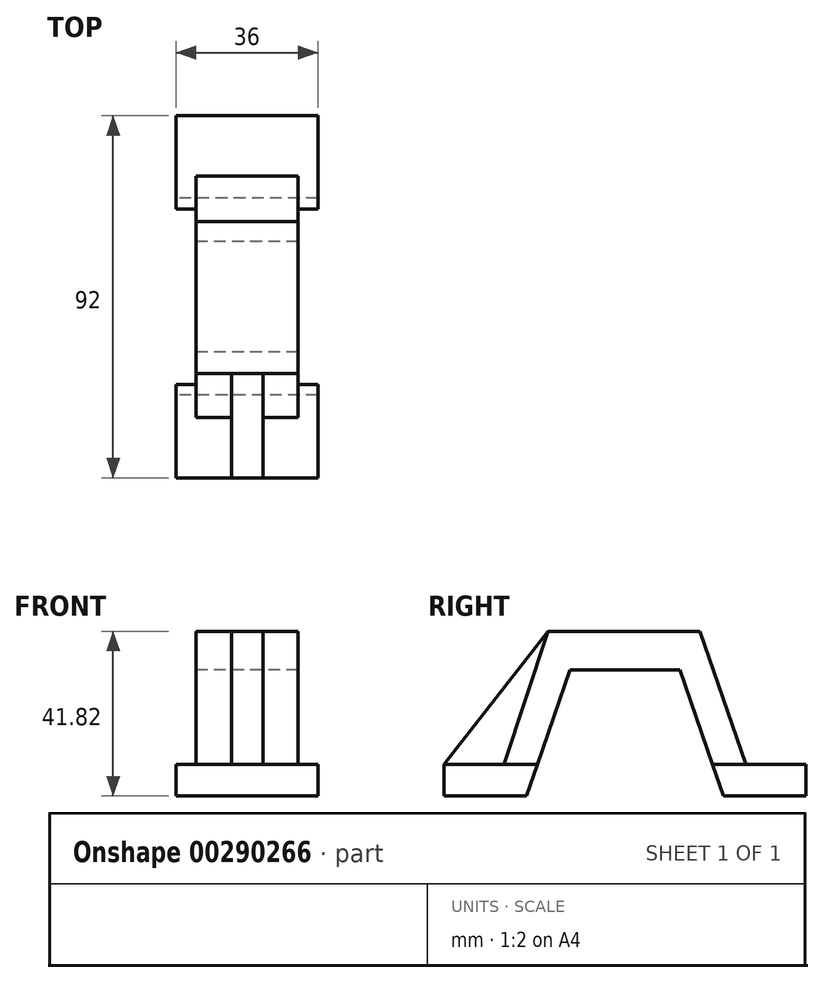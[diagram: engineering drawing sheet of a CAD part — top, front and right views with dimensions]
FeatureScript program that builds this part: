
annotation { "Feature Type Name" : "Feature", "Feature Type Description" : "" }
export const myFeature = defineFeature(function(context is Context, id is Id, definition is map)
    precondition{}
    {
        {
            var Q0;
            Q0=qCreatedBy(makeId("Right.planeOp"),FACE);
            var sketch = newSketch(context, id + "F0", { "sketchPlane" : qUnion([Q0])});
            skLineSegment(sketch, "E0", {"start": v(-64.15, 0) * mm, "end": v(-43.15, 0) * mm});
            skLineSegment(sketch, "E1", {"start": v(6.85, 0) * mm, "end": v(27.85, 0) * mm});
            skLineSegment(sketch, "E2", {"start": v(-32.15, 32) * mm, "end": v(-43.15, 0) * mm});
            skLineSegment(sketch, "E3", {"start": v(-32.15, 32) * mm, "end": v(-4.15, 32) * mm});
            skLineSegment(sketch, "E4", {"start": v(-4.15, 32) * mm, "end": v(6.85, 0) * mm});
            skLineSegment(sketch, "E5", {"start": v(-64.15, 0) * mm, "end": v(-64.15, 8) * mm});
            skLineSegment(sketch, "E6", {"start": v(-48.86, 8) * mm, "end": v(-64.15, 8) * mm});
            skLineSegment(sketch, "E7", {"start": v(-48.86, 8) * mm, "end": v(-37.69, 41.82) * mm});
            skLineSegment(sketch, "E8", {"start": v(-37.69, 41.82) * mm, "end": v(0.94, 41.82) * mm});
            skLineSegment(sketch, "E9", {"start": v(27.85, 0) * mm, "end": v(27.85, 8) * mm});
            skLineSegment(sketch, "E10", {"start": v(0.94, 41.82) * mm, "end": v(12.56, 8) * mm});
            skLineSegment(sketch, "E11", {"start": v(12.56, 8) * mm, "end": v(27.85, 8) * mm});
            skLineSegment(sketch, "E12", {"start": v(-64.15, 8) * mm, "end": v(-37.69, 41.82) * mm});
            skLineSegment(sketch, "E13", {"start": v(0.94, 41.82) * mm, "end": v(0.94, 66.82) * mm});
            skLineSegment(sketch, "E14", {"start": v(0.94, 66.82) * mm, "end": v(-28.06, 66.82) * mm});
            skLineSegment(sketch, "E15", {"start": v(-28.06, 66.82) * mm, "end": v(-28.06, 41.82) * mm});
            skSolve(sketch);
        }
        {
            var Q0;
            Q0=makeQuery(id+"F0.imprint","IMPRINT",FACE,{"disambiguationData":[TD([[makeQuery(id+"F0.imprint","IMPRINT",EDGE,{"derivedFrom":sQuery(id+"F0.wireOp",EDGE,"E0")}),1.0]])]});
            extrude(context, id + "F1", {"entities" : qUnion([Q0]), "depth" : 36 * mm});
        }
        {
            var Q0;
            Q0=makeQuery(id+"F1.opExtrude","CAP_FACE",FACE,{"disambiguationData":[OSD([sQuery(id+"F0.wireOp",EDGE,"E0"),sQuery(id+"F0.wireOp",EDGE,"E1"),sQuery(id+"F0.wireOp",EDGE,"E2"),sQuery(id+"F0.wireOp",EDGE,"E3"),sQuery(id+"F0.wireOp",EDGE,"E4"),sQuery(id+"F0.wireOp",EDGE,"E5"),sQuery(id+"F0.wireOp",EDGE,"E6"),sQuery(id+"F0.wireOp",EDGE,"E7"),sQuery(id+"F0.wireOp",EDGE,"E8"),sQuery(id+"F0.wireOp",EDGE,"E9"),sQuery(id+"F0.wireOp",EDGE,"E10"),sQuery(id+"F0.wireOp",EDGE,"E11")])],"isStart":false});
            var sketch = newSketch(context, id + "F2", { "sketchPlane" : qUnion([Q0])});
            skLineSegment(sketch, "E16", {"start": v(-48.86, 8) * mm, "end": v(-40.4, 8) * mm});
            skLineSegment(sketch, "E17", {"start": v(12.56, 8) * mm, "end": v(4.1, 8) * mm});
            skLineSegment(sketch, "E18", {"start": v(-48.86, 8) * mm, "end": v(-37.69, 41.82) * mm});
            skLineSegment(sketch, "E19", {"start": v(-37.69, 41.82) * mm, "end": v(0.94, 41.82) * mm});
            skLineSegment(sketch, "E20", {"start": v(0.94, 41.82) * mm, "end": v(12.56, 8) * mm});
            skLineSegment(sketch, "E21", {"start": v(4.1, 8) * mm, "end": v(-4.15, 32) * mm});
            skLineSegment(sketch, "E22", {"start": v(-4.15, 32) * mm, "end": v(-32.15, 32) * mm});
            skLineSegment(sketch, "E23", {"start": v(-32.15, 32) * mm, "end": v(-40.4, 8) * mm});
            skSolve(sketch);
        }
        {
            var Q0;
            Q0=makeQuery(id+"F2.imprint","IMPRINT",FACE,{"disambiguationData":[TD([[makeQuery(id+"F2.imprint","IMPRINT",EDGE,{"derivedFrom":sQuery(id+"F2.wireOp",EDGE,"E16")}),1.0]])]});
            extrude(context, id + "F3", {"entities" : qUnion([Q0]), "operationType" : NewBodyOperationType.REMOVE, "oppositeDirection" : true, "depth" : 5 * mm});
        }
        {
            var Q0;
            Q0=makeQuery(id+"F1.opExtrude","CAP_FACE",FACE,{"disambiguationData":[OSD([sQuery(id+"F0.wireOp",EDGE,"E0"),sQuery(id+"F0.wireOp",EDGE,"E1"),sQuery(id+"F0.wireOp",EDGE,"E2"),sQuery(id+"F0.wireOp",EDGE,"E3"),sQuery(id+"F0.wireOp",EDGE,"E4"),sQuery(id+"F0.wireOp",EDGE,"E5"),sQuery(id+"F0.wireOp",EDGE,"E6"),sQuery(id+"F0.wireOp",EDGE,"E7"),sQuery(id+"F0.wireOp",EDGE,"E8"),sQuery(id+"F0.wireOp",EDGE,"E9"),sQuery(id+"F0.wireOp",EDGE,"E10"),sQuery(id+"F0.wireOp",EDGE,"E11")])],"isStart":true});
            var sketch = newSketch(context, id + "F4", { "sketchPlane" : qUnion([Q0])});
            skLineSegment(sketch, "E24", {"start": v(-12.56, 8) * mm, "end": v(-4.1, 8) * mm});
            skLineSegment(sketch, "E25", {"start": v(-4.1, 8) * mm, "end": v(4.15, 32) * mm});
            skLineSegment(sketch, "E26", {"start": v(4.15, 32) * mm, "end": v(32.15, 32) * mm});
            skLineSegment(sketch, "E27", {"start": v(32.15, 32) * mm, "end": v(40.4, 8) * mm});
            skLineSegment(sketch, "E28", {"start": v(40.4, 8) * mm, "end": v(48.86, 8) * mm});
            skLineSegment(sketch, "E29", {"start": v(48.86, 8) * mm, "end": v(37.69, 41.82) * mm});
            skLineSegment(sketch, "E30", {"start": v(37.69, 41.82) * mm, "end": v(-0.94, 41.82) * mm});
            skLineSegment(sketch, "E31", {"start": v(-0.94, 41.82) * mm, "end": v(-12.56, 8) * mm});
            skSolve(sketch);
        }
        {
            var Q0;
            Q0=makeQuery(id+"F4.imprint","IMPRINT",FACE,{"disambiguationData":[TD([[makeQuery(id+"F4.imprint","IMPRINT",EDGE,{"derivedFrom":sQuery(id+"F4.wireOp",EDGE,"E24")}),1.0]])]});
            extrude(context, id + "F5", {"entities" : qUnion([Q0]), "operationType" : NewBodyOperationType.REMOVE, "oppositeDirection" : true, "depth" : 5 * mm});
        }
        {
            var Q0;
            Q0=makeQuery(id+"F0.imprint","IMPRINT",FACE,{"disambiguationData":[TD([[makeQuery(id+"F0.imprint","IMPRINT",EDGE,{"derivedFrom":sQuery(id+"F0.wireOp",EDGE,"E6")}),-1.0]])]});
            extrude(context, id + "F6", {"entities" : qUnion([Q0]), "operationType" : NewBodyOperationType.ADD, "depth" : 22 * mm});
        }
        {
            var Q0;
            Q0=makeQuery(id+"F0.imprint","IMPRINT",FACE,{"disambiguationData":[TD([[makeQuery(id+"F0.imprint","IMPRINT",EDGE,{"derivedFrom":sQuery(id+"F0.wireOp",EDGE,"E6")}),-1.0]])]});
            extrude(context, id + "F7", {"entities" : qUnion([Q0]), "operationType" : NewBodyOperationType.REMOVE, "depth" : 14 * mm});
        }
    });
